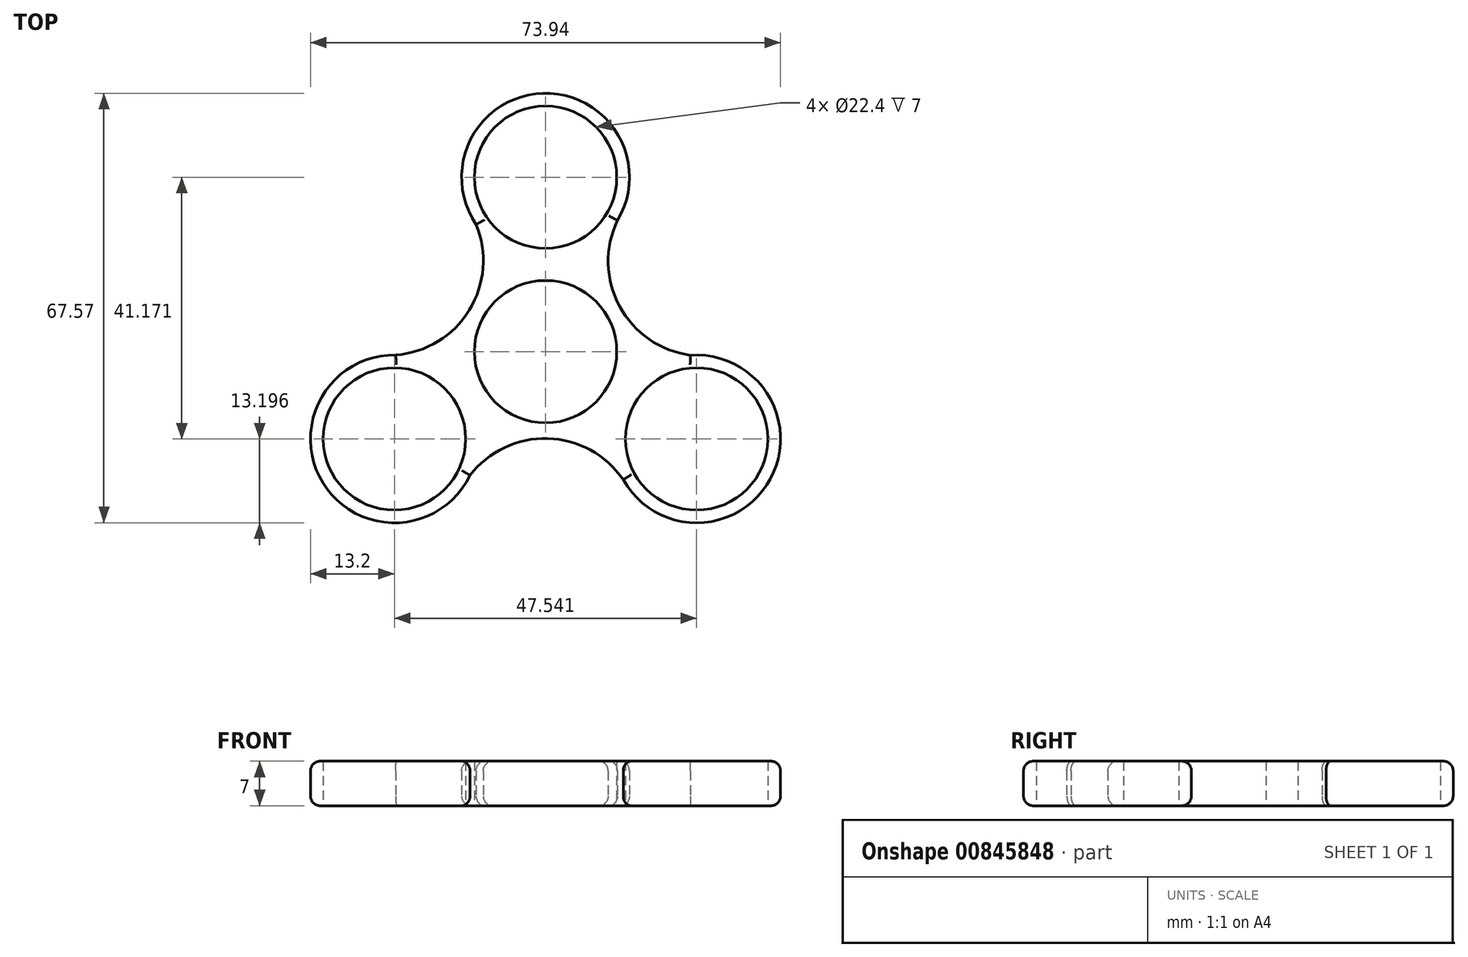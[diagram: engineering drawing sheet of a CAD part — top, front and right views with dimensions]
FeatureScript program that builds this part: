
annotation { "Feature Type Name" : "Feature", "Feature Type Description" : "" }
export const myFeature = defineFeature(function(context is Context, id is Id, definition is map)
    precondition{}
    {
        {
            var Q0;
            Q0=qCreatedBy(makeId("Top.planeOp"),FACE);
            var sketch = newSketch(context, id + "F0", { "sketchPlane" : qUnion([Q0])});
            skCircle(sketch, "E0", {"center": v(0, 0) * mm, "radius": 11.2 * mm});
            skCircle(sketch, "E1", {"center": v(0, 27.45) * mm, "radius": 11.2 * mm});
            skArc(sketch, "E2", {"start": v(11.32, 20.65) * mm, "mid": v(-0.38, 40.64) * mm, "end": v(-10.9, 20.02) * mm});
            skArc(sketch, "E3.1.0", {"start": v(-23.54, -0.53) * mm, "mid": v(-35, -20.65) * mm, "end": v(-11.88, -19.46) * mm});
            skCircle(sketch, "E3.1.1", {"center": v(-23.77, -13.72) * mm, "radius": 11.2 * mm});
            skArc(sketch, "E3.2.0", {"start": v(12.23, -20.13) * mm, "mid": v(35.39, -20) * mm, "end": v(22.8, -0.56) * mm});
            skCircle(sketch, "E3.2.1", {"center": v(23.77, -13.72) * mm, "radius": 11.2 * mm});
            skArc(sketch, "E4", {"start": v(11.32, 20.65) * mm, "mid": v(11.66, 7.13) * mm, "end": v(22.8, -0.56) * mm});
            skArc(sketch, "E5.1.0", {"start": v(-23.54, -0.53) * mm, "mid": v(-12, 6.53) * mm, "end": v(-10.9, 20.02) * mm});
            skArc(sketch, "E5.2.0", {"start": v(12.23, -20.13) * mm, "mid": v(0.34, -13.66) * mm, "end": v(-11.88, -19.46) * mm});
            skSolve(sketch);
        }
        {
            var Q0;
            Q0=makeQuery(id+"F0.imprint","IMPRINT",FACE,{"disambiguationData":[TD([[makeQuery(id+"F0.imprint","IMPRINT",EDGE,{"derivedFrom":sQuery(id+"F0.wireOp",EDGE,"E0")}),-1.0]])]});
            extrude(context, id + "F1", {"entities" : qUnion([Q0]), "depth" : 7 * mm, "offsetDistance" : 25 * mm});
        }
        {
            var Q0;
            Q0=makeQuery(id+"F1.opExtrude","CAP_EDGE",EDGE,{"disambiguationData":[OSD([sQuery(id+"F0.wireOp",EDGE,"E3.1.0")])],"isStart":false});
            var Q1;
            Q1=makeQuery(id+"F1.opExtrude","CAP_EDGE",EDGE,{"disambiguationData":[OSD([sQuery(id+"F0.wireOp",EDGE,"E5.2.0")])],"isStart":false});
            var Q2;
            Q2=makeQuery(id+"F1.opExtrude","CAP_EDGE",EDGE,{"disambiguationData":[OSD([sQuery(id+"F0.wireOp",EDGE,"E2")])],"isStart":false});
            var Q3;
            Q3=makeQuery(id+"F1.opExtrude","CAP_EDGE",EDGE,{"disambiguationData":[OSD([sQuery(id+"F0.wireOp",EDGE,"E5.1.0")])],"isStart":false});
            var Q4;
            Q4=makeQuery(id+"F1.opExtrude","CAP_EDGE",EDGE,{"disambiguationData":[OSD([sQuery(id+"F0.wireOp",EDGE,"E4")])],"isStart":false});
            var Q5;
            Q5=makeQuery(id+"F1.opExtrude","CAP_EDGE",EDGE,{"disambiguationData":[OSD([sQuery(id+"F0.wireOp",EDGE,"E3.2.0")])],"isStart":false});
            var Q6;
            Q6=makeQuery(id+"F1.opExtrude","CAP_EDGE",EDGE,{"disambiguationData":[OSD([sQuery(id+"F0.wireOp",EDGE,"E2")])],"isStart":true});
            var Q7;
            Q7=makeQuery(id+"F1.opExtrude","CAP_EDGE",EDGE,{"disambiguationData":[OSD([sQuery(id+"F0.wireOp",EDGE,"E5.1.0")])],"isStart":true});
            var Q8;
            Q8=makeQuery(id+"F1.opExtrude","CAP_EDGE",EDGE,{"disambiguationData":[OSD([sQuery(id+"F0.wireOp",EDGE,"E3.1.0")])],"isStart":true});
            var Q9;
            Q9=makeQuery(id+"F1.opExtrude","CAP_EDGE",EDGE,{"disambiguationData":[OSD([sQuery(id+"F0.wireOp",EDGE,"E5.2.0")])],"isStart":true});
            var Q10;
            Q10=makeQuery(id+"F1.opExtrude","CAP_EDGE",EDGE,{"disambiguationData":[OSD([sQuery(id+"F0.wireOp",EDGE,"E3.2.0")])],"isStart":true});
            var Q11;
            Q11=makeQuery(id+"F1.opExtrude","CAP_EDGE",EDGE,{"disambiguationData":[OSD([sQuery(id+"F0.wireOp",EDGE,"E4")])],"isStart":true});
            fillet(context, id + "F2", {"entities" : qUnion([Q0, Q1, Q2, Q3, Q4, Q5, Q6, Q7, Q8, Q9, Q10, Q11]), "radius" : 1.5 * mm, "tangentPropagation" : true, "allowEdgeOverflow" : false});
        }
    });
